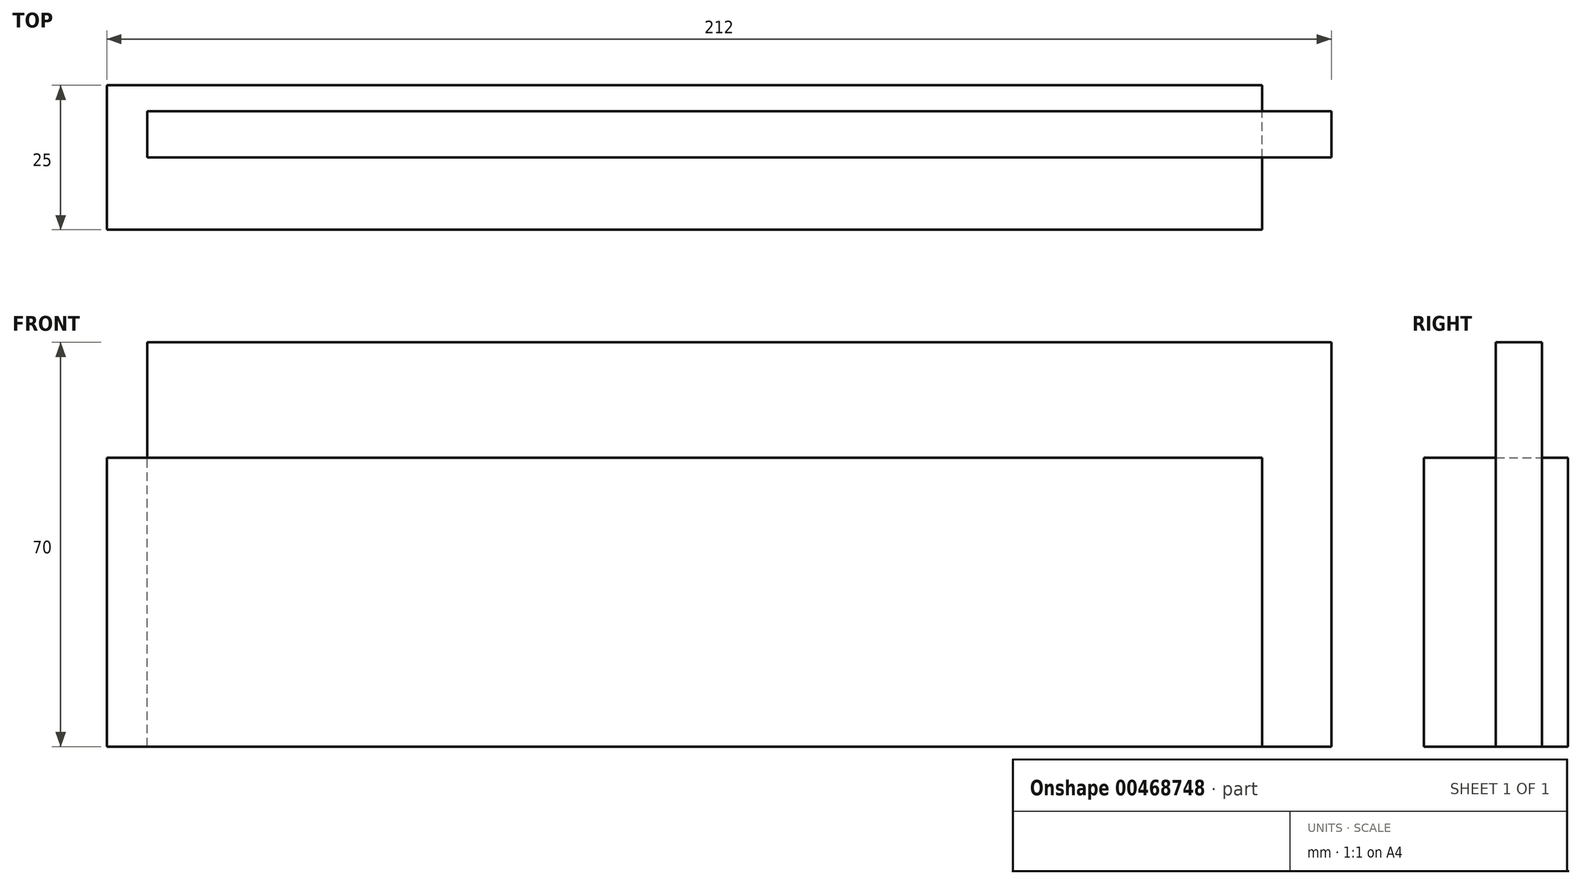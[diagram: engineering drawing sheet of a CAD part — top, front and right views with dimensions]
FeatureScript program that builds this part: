
annotation { "Feature Type Name" : "Feature", "Feature Type Description" : "" }
export const myFeature = defineFeature(function(context is Context, id is Id, definition is map)
    precondition{}
    {
        {
            var Q0;
            Q0=qCreatedBy(makeId("Front.planeOp"),FACE);
            var sketch = newSketch(context, id + "F0", { "sketchPlane" : qUnion([Q0])});
            skLineSegment(sketch, "E0.bottom", {"start": v(100, 25) * mm, "end": v(-100, 25) * mm});
            skLineSegment(sketch, "E0.top", {"start": v(100, -25) * mm, "end": v(-100, -25) * mm});
            skLineSegment(sketch, "E0.left", {"start": v(100, 25) * mm, "end": v(100, -25) * mm});
            skLineSegment(sketch, "E0.right", {"start": v(-100, 25) * mm, "end": v(-100, -25) * mm});
            skPoint(sketch, "E0.middle", {"position": v(0, 0) * mm});
            skSolve(sketch);
        }
        {
            var Q0;
            Q0=qSketchRegion(id+"F0",true);
            extrude(context, id + "F1", {"entities" : qUnion([Q0]), "endBound" : BoundingType.SYMMETRIC, "depth" : 25 * mm});
        }
        {
            var Q0;
            Q0=qCreatedBy(makeId("Front.planeOp"),FACE);
            var sketch = newSketch(context, id + "F2", { "sketchPlane" : qUnion([Q0])});
            skLineSegment(sketch, "E1.0.0", {"start": v(-100, -25) * mm, "end": v(100, -25) * mm, "construction": true});
            skLineSegment(sketch, "E1.0.1", {"start": v(100, -25) * mm, "end": v(100, 25) * mm, "construction": true});
            skLineSegment(sketch, "E1.0.2", {"start": v(100, 25) * mm, "end": v(-100, 25) * mm, "construction": true});
            skLineSegment(sketch, "E1.0.3", {"start": v(-100, 25) * mm, "end": v(-100, -25) * mm, "construction": true});
            skLineSegment(sketch, "E2.bottom", {"start": v(-93, -25) * mm, "end": v(112, -25) * mm});
            skLineSegment(sketch, "E2.top", {"start": v(-93, 45) * mm, "end": v(112, 45) * mm});
            skLineSegment(sketch, "E2.left", {"start": v(-93, -25) * mm, "end": v(-93, 45) * mm});
            skLineSegment(sketch, "E2.right", {"start": v(112, -25) * mm, "end": v(112, 45) * mm});
            skSolve(sketch);
        }
        {
            var Q0;
            Q0=qSketchRegion(id+"F2",true);
            extrude(context, id + "F3", {"entities" : qUnion([Q0]), "oppositeDirection" : true, "depth" : 8 * mm});
        }
    });
